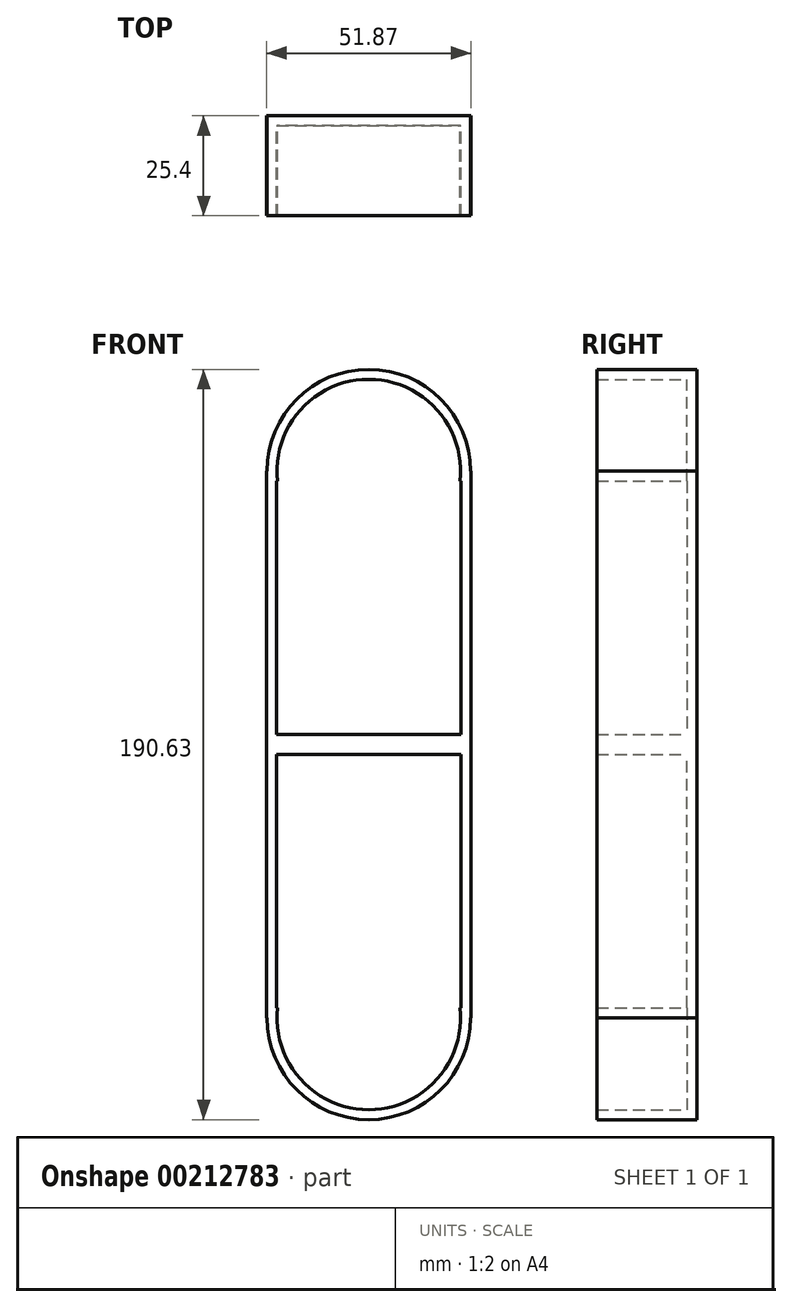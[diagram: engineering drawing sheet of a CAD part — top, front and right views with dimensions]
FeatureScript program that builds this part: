
annotation { "Feature Type Name" : "Feature", "Feature Type Description" : "" }
export const myFeature = defineFeature(function(context is Context, id is Id, definition is map)
    precondition{}
    {
        {
            var Q0;
            Q0=qCreatedBy(makeId("Front.planeOp"),FACE);
            var sketch = newSketch(context, id + "F0", { "sketchPlane" : qUnion([Q0])});
            skLineSegment(sketch, "E0.bottom", {"start": v(-24.38, 13.66) * mm, "end": v(27.5, 13.66) * mm});
            skLineSegment(sketch, "E0.top", {"start": v(-24.38, -55.81) * mm, "end": v(27.5, -55.81) * mm});
            skLineSegment(sketch, "E0.left", {"start": v(-24.38, 13.66) * mm, "end": v(-24.38, -55.81) * mm});
            skLineSegment(sketch, "E0.right", {"start": v(27.5, 13.66) * mm, "end": v(27.5, -55.81) * mm});
            skArc(sketch, "E1", {"start": v(27.4, 13.66) * mm, "mid": v(1.56, 39.5) * mm, "end": v(-24.3, 13.66) * mm});
            skSolve(sketch);
        }
        {
            var Q0;
            Q0 = qSketchRegion(id + "F0", true);
            extrude(context, id + "F1", {"entities" : qUnion([Q0]), "depth" : 25.4 * mm});
        }
        {
            var Q0;
            Q0=makeQuery(id+"F1.opExtrude","CAP_FACE",FACE,{"disambiguationData":[OSD([sQuery(id+"F0.wireOp",EDGE,"E0.bottom"),sQuery(id+"F0.wireOp",EDGE,"E0.top"),sQuery(id+"F0.wireOp",EDGE,"E0.left"),sQuery(id+"F0.wireOp",EDGE,"E0.right"),sQuery(id+"F0.wireOp",EDGE,"E1")])],"isStart":false});
            var sketch = newSketch(context, id + "F2", { "sketchPlane" : qUnion([Q0])});
            skLineSegment(sketch, "E2.bottom", {"start": v(-20.63, 15.75) * mm, "end": v(-20.24, 15.75) * mm});
            skLineSegment(sketch, "E2.top", {"start": v(-20.63, -52.04) * mm, "end": v(23.79, -52.04) * mm});
            skLineSegment(sketch, "E2.left", {"start": v(-20.63, 15.75) * mm, "end": v(-20.63, -52.04) * mm});
            skLineSegment(sketch, "E2.right", {"start": v(23.79, 15.75) * mm, "end": v(23.79, -52.04) * mm});
            skArc(sketch, "E3", {"start": v(23.4, 15.75) * mm, "mid": v(1.58, 37.57) * mm, "end": v(-20.24, 15.75) * mm});
            skLineSegment(sketch, "E4.trimOffspring", {"start": v(23.4, 15.75) * mm, "end": v(23.79, 15.75) * mm});
            skSolve(sketch);
        }
        {
            var Q0;
            Q0=makeQuery(id+"F1.opExtrude","CAP_FACE",FACE,{"disambiguationData":[OSD([sQuery(id+"F0.wireOp",EDGE,"E0.bottom"),sQuery(id+"F0.wireOp",EDGE,"E0.top"),sQuery(id+"F0.wireOp",EDGE,"E0.left"),sQuery(id+"F0.wireOp",EDGE,"E0.right"),sQuery(id+"F0.wireOp",EDGE,"E1")])],"isStart":false});
            shell(context, id + "F3", {"entities" : qUnion([Q0]), "thickness" : 2.54 * mm});
        }
        {
            var Q0;
            Q0=makeQuery(id+"F1.opExtrude","SWEPT_BODY",BODY,{"disambiguationData":[OSD([sQuery(id+"F0.wireOp",EDGE,"E0.bottom"),sQuery(id+"F0.wireOp",EDGE,"E0.top"),sQuery(id+"F0.wireOp",EDGE,"E0.left"),sQuery(id+"F0.wireOp",EDGE,"E0.right"),sQuery(id+"F0.wireOp",EDGE,"E1")])]});
            var Q1;
            Q1=makeQuery(id+"F1.opExtrude","SWEPT_FACE",FACE,{"disambiguationData":[OSD([sQuery(id+"F0.wireOp",EDGE,"E0.top")])]});
            mirror(context, id + "F4", {"operationType" : NewBodyOperationType.ADD, "entities" : qUnion([Q0]), "mirrorPlane" : qUnion([Q1])});
        }
    });
